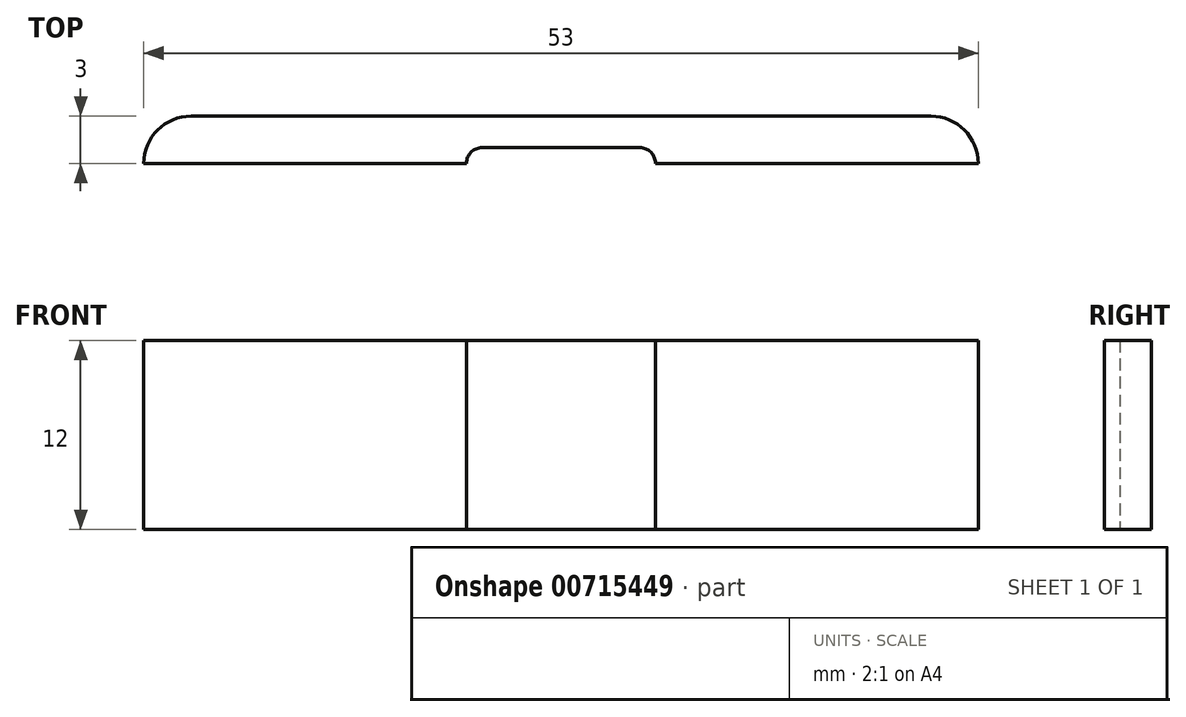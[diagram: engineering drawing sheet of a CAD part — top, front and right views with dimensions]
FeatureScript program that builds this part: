
annotation { "Feature Type Name" : "Feature", "Feature Type Description" : "" }
export const myFeature = defineFeature(function(context is Context, id is Id, definition is map)
    precondition{}
    {
        {
            var Q0;
            Q0=qCreatedBy(makeId("Top.planeOp"),FACE);
            var sketch = newSketch(context, id + "F0", { "sketchPlane" : qUnion([Q0])});
            skLineSegment(sketch, "E0", {"start": v(5.88, 1.16) * mm, "end": v(5.88, -1.84) * mm});
            skLineSegment(sketch, "E1", {"start": v(5.88, -1.84) * mm, "end": v(26.38, -1.84) * mm});
            skLineSegment(sketch, "E2", {"start": v(26.38, -1.84) * mm, "end": v(26.38, -0.84) * mm});
            skLineSegment(sketch, "E3", {"start": v(26.38, -0.84) * mm, "end": v(38.38, -0.84) * mm});
            skLineSegment(sketch, "E4", {"start": v(38.38, -0.84) * mm, "end": v(38.38, -1.84) * mm});
            skLineSegment(sketch, "E5", {"start": v(38.38, -1.84) * mm, "end": v(58.88, -1.84) * mm});
            skLineSegment(sketch, "E6", {"start": v(58.88, -1.84) * mm, "end": v(58.88, 1.16) * mm});
            skLineSegment(sketch, "E7", {"start": v(58.88, 1.16) * mm, "end": v(41.38, 1.16) * mm});
            skLineSegment(sketch, "E8", {"start": v(41.38, 1.16) * mm, "end": v(41.38, 1.16) * mm});
            skLineSegment(sketch, "E9", {"start": v(41.38, 1.16) * mm, "end": v(23.38, 1.16) * mm});
            skLineSegment(sketch, "E10", {"start": v(23.38, 1.16) * mm, "end": v(23.38, 1.16) * mm});
            skLineSegment(sketch, "E11", {"start": v(23.38, 1.16) * mm, "end": v(5.88, 1.16) * mm});
            skSolve(sketch);
        }
        {
            var Q0;
            Q0=makeQuery(id+"F0.imprint","IMPRINT",FACE,{"disambiguationData":[TD([[makeQuery(id+"F0.imprint","IMPRINT",EDGE,{"derivedFrom":sQuery(id+"F0.wireOp",EDGE,"E0")}),1.0]])]});
            extrude(context, id + "F1", {"entities" : qUnion([Q0]), "depth" : 12 * mm, "offsetDistance" : 25 * mm});
        }
        {
            var Q0;
            Q0=makeQuery(id+"F1.opExtrude","SWEPT_EDGE",EDGE,{"disambiguationData":[OSD([sQuery(id+"F0.wireOp",EDGE,"E3"),sQuery(id+"F0.wireOp",EDGE,"E4")])]});
            var Q1;
            Q1=makeQuery(id+"F1.opExtrude","SWEPT_EDGE",EDGE,{"disambiguationData":[OSD([sQuery(id+"F0.wireOp",EDGE,"E2"),sQuery(id+"F0.wireOp",EDGE,"E3")])]});
            fillet(context, id + "F2", {"entities" : qUnion([Q0, Q1]), "tangentPropagation" : true, "radius" : 1 * mm, "defaultsChanged" : true, "vertexSettings" : [], "allowEdgeOverflow" : false});
        }
        {
            var Q0;
            Q0=makeQuery(id+"F1.opExtrude","SWEPT_EDGE",EDGE,{"disambiguationData":[OSD([sQuery(id+"F0.wireOp",EDGE,"E0"),sQuery(id+"F0.wireOp",EDGE,"E11")])]});
            var Q1;
            Q1=makeQuery(id+"F1.opExtrude","SWEPT_EDGE",EDGE,{"disambiguationData":[OSD([sQuery(id+"F0.wireOp",EDGE,"E6"),sQuery(id+"F0.wireOp",EDGE,"E7")])]});
            fillet(context, id + "F3", {"entities" : qUnion([Q0, Q1]), "tangentPropagation" : true, "radius" : 3 * mm, "defaultsChanged" : true, "vertexSettings" : [], "allowEdgeOverflow" : false});
        }
    });
